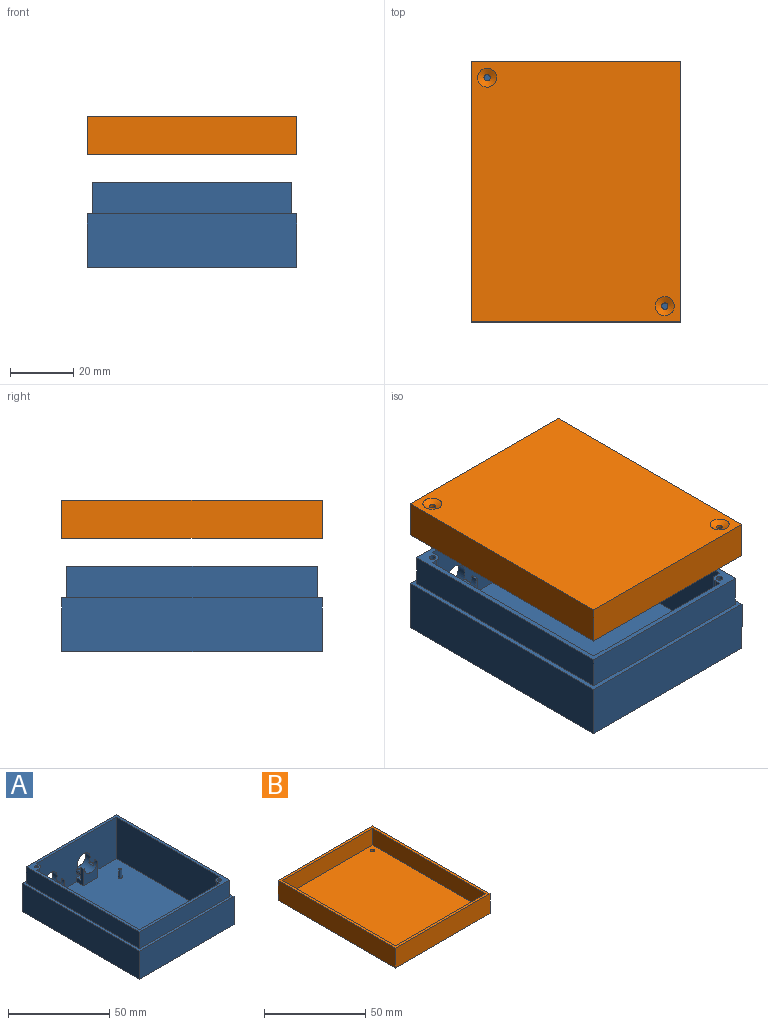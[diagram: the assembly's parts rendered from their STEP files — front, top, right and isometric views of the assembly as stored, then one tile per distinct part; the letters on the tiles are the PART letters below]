
ASSEMBLY  parts=2 mates=1
PART A: 68 faces, bbox 66x82x27 mm
  f0: plane 10x5mm, normal (-1,0,0), area 30.7mm2, adj f6,f7,f10,f11,f40,f46,f47,f49
  f1: plane 10x5mm, normal (1,0,0), area 30.7mm2, adj f6,f10,f11,f37,f39,f46,f47,f57
  f2: plane 10x5mm, normal (-1,0,0), area 30.7mm2, adj f8,f9,f10,f11,f42,f44,f45,f55
  f3: plane 10x5mm, normal (1,0,0), area 30.7mm2, adj f8,f10,f11,f38,f41,f44,f45,f50
  f4: cylinder r=4.5mm len=9mm, axis (0,-1,0), area 137.2mm2, adj f8,f9,f11,f35,f38,f41,f42,f53
  f5: cylinder r=4.5mm len=9mm, axis (0,-1,0), area 137.2mm2, adj f6,f7,f11,f35,f37,f39,f40,f51
  f6: plane 10x10mm, normal (0,-1,0), area 68.2mm2, adj f0,f1,f5,f7,f10,f37
  f7: plane 2x0.5mm, normal (0,0,1), area 1mm2, adj f0,f5,f6,f40
  f8: plane 10x10mm, normal (0,-1,0), area 68.2mm2, adj f2,f3,f4,f9,f10,f38
  f9: plane 2x0.5mm, normal (0,0,1), area 1mm2, adj f2,f4,f8,f42
  f10: plane 76x60mm, normal (0,0,1), area 4417.2mm2, adj f0,f1,f2,f3,f6,f8,f11,f12
  f11: plane 56x25mm, normal (0,-1,0), area 1185.4mm2, adj f0,f1,f2,f3,f4,f5,f10,f20
  f12: cone r=1mm half-angle=3deg, axis (0,0,-1), area 27.3mm2, adj f10,f13
  f13: plane 1.48x1.48mm, normal (0,0,1), area 1.7mm2, adj f12
  f14: cone r=1mm half-angle=3deg, axis (0,0,-1), area 27.3mm2, adj f10,f15
  f15: plane 1.48x1.48mm, normal (0,0,1), area 1.7mm2, adj f14
  f16: cone r=1mm half-angle=3deg, axis (0,0,-1), area 27.3mm2, adj f10,f17
  f17: plane 1.48x1.48mm, normal (0,0,1), area 1.7mm2, adj f16
  f18: cone r=1mm half-angle=3deg, axis (0,0,-1), area 27.3mm2, adj f10,f19
  f19: plane 1.48x1.48mm, normal (0,0,1), area 1.7mm2, adj f18
  f20: plane 25x2mm, normal (1,0,0), area 50mm2, adj f10,f11,f29,f61
  f21: plane 72x25mm, normal (-1,0,0), area 1800mm2, adj f10,f11,f22,f29
  f22: plane 25x2mm, normal (0,1,0), area 50mm2, adj f10,f21,f29,f62
  f23: plane 25x2mm, normal (-1,0,0), area 50mm2, adj f10,f24,f29,f62
  f24: plane 56x25mm, normal (0,1,0), area 1400mm2, adj f10,f23,f25,f29
  f25: plane 72x25mm, normal (1,0,0), area 1800mm2, adj f10,f24,f27,f29
  f26: cylinder r=1mm len=25mm, axis (0,0,-1), area 157.1mm2, adj f29,f31
  f27: plane 25x2mm, normal (0,-1,0), area 50mm2, adj f10,f25,f29,f61
  f28: cylinder r=1mm len=25mm, axis (0,0,-1), area 157.1mm2, adj f29,f30
  f29: plane 79x63mm, normal (0,0,1), area 441mm2, adj f11,f20,f21,f22,f23,f24,f25,f26
  f30: plane 2x2mm, normal (0,0,1), area 3.1mm2, adj f28
  f31: plane 2x2mm, normal (0,0,1), area 3.1mm2, adj f26
  f32: plane 82x66mm, normal (0,0,-1), area 5412mm2, adj f33,f34,f35,f36
  f33: plane 66x17mm, normal (0,-1,0), area 1122mm2, adj f32,f34,f36,f67
  f34: plane 82x17mm, normal (-1,0,0), area 1394mm2, adj f32,f33,f35,f67
  f35: plane 66x17mm, normal (0,1,0), area 994.8mm2, adj f4,f5,f32,f34,f36,f67
  f36: plane 82x17mm, normal (1,0,0), area 1394mm2, adj f32,f33,f35,f67
  f37: plane 2x0.5mm, normal (0,0,1), area 1mm2, adj f1,f5,f6,f39
  f38: plane 2x0.5mm, normal (0,0,1), area 1mm2, adj f3,f4,f8,f41
  f39: plane 3.45x1.5mm, normal (0,1,0), area 2mm2, adj f1,f5,f37,f57,f58
  f40: plane 3.45x1.5mm, normal (0,1,0), area 2mm2, adj f0,f5,f7,f51,f52
  f41: plane 3.45x1.5mm, normal (0,1,0), area 2mm2, adj f3,f4,f38,f53,f54
  f42: plane 3.45x1.5mm, normal (0,1,0), area 2mm2, adj f2,f4,f9,f55,f56
  f43: plane 8x3mm, normal (0,0,-1), area 24mm2, adj f11,f45,f50,f60
  f44: plane 10x3mm, normal (0,0,1), area 30mm2, adj f2,f3,f11,f45
  f45: plane 10x3mm, normal (0,1,0), area 20.4mm2, adj f2,f3,f43,f44,f50,f60
  f46: plane 10x3mm, normal (0,1,0), area 20.4mm2, adj f0,f1,f47,f48,f49,f59
  f47: plane 10x3mm, normal (0,0,1), area 30mm2, adj f0,f1,f11,f46
  f48: plane 8x3mm, normal (0,0,-1), area 24mm2, adj f11,f46,f49,f59
  f49: cylinder r=1mm len=3mm, axis (0,-1,0), area 4.7mm2, adj f0,f11,f46,f48
  f50: cylinder r=1mm len=3mm, axis (0,1,0), area 4.7mm2, adj f3,f11,f43,f45
  f51: cylinder r=1mm len=3mm, axis (0,-1,0), area 2.3mm2, adj f5,f11,f40,f52
  f52: cylinder r=1mm len=3mm, axis (0,1,0), area 4.3mm2, adj f0,f11,f40,f51
  f53: cylinder r=1mm len=3mm, axis (0,-1,0), area 2.3mm2, adj f4,f11,f41,f54
  f54: cylinder r=1mm len=3mm, axis (0,-1,0), area 4.3mm2, adj f3,f11,f41,f53
  f55: cylinder r=1mm len=3mm, axis (0,1,0), area 4.3mm2, adj f2,f11,f42,f56
  f56: cylinder r=1mm len=3mm, axis (0,-1,0), area 2.3mm2, adj f4,f11,f42,f55
  f57: cylinder r=1mm len=3mm, axis (0,-1,0), area 4.3mm2, adj f1,f11,f39,f58
  f58: cylinder r=1mm len=3mm, axis (0,-1,0), area 2.3mm2, adj f5,f11,f39,f57
  f59: cylinder r=1mm len=3mm, axis (0,1,0), area 4.7mm2, adj f1,f11,f46,f48
  f60: cylinder r=1mm len=3mm, axis (0,-1,0), area 4.7mm2, adj f2,f11,f43,f45
  f61: cylinder r=2mm len=25mm, axis (0,0,1), area 78.5mm2, adj f10,f20,f27,f29
  f62: cylinder r=2mm len=25mm, axis (0,0,1), area 78.5mm2, adj f10,f22,f23,f29
  f63: plane 79x10mm, normal (-1,0,0), area 790mm2, adj f29,f64,f66,f67
  f64: plane 63x10mm, normal (0,1,0), area 630mm2, adj f29,f63,f65,f67
  f65: plane 79x10mm, normal (1,0,0), area 790mm2, adj f29,f64,f66,f67
  f66: plane 63x10mm, normal (0,-1,0), area 630mm2, adj f29,f63,f65,f67
  f67: plane 82x66mm, normal (0,0,1), area 435mm2, adj f33,f34,f35,f36,f63,f64,f65,f66
PART B: 15 faces, bbox 66x82x12 mm
  f0: plane 79x10mm, normal (1,0,0), area 790mm2, adj f1,f7,f8,f9
  f1: plane 63x10mm, normal (0,-1,0), area 630mm2, adj f0,f2,f8,f9
  f2: plane 79x10mm, normal (-1,0,0), area 790mm2, adj f1,f7,f8,f9
  f3: plane 82x12mm, normal (-1,0,0), area 984mm2, adj f4,f6,f8,f12
  f4: plane 66x12mm, normal (0,-1,0), area 792mm2, adj f3,f5,f8,f12
  f5: plane 82x12mm, normal (1,0,0), area 984mm2, adj f4,f6,f8,f12
  f6: plane 66x12mm, normal (0,1,0), area 792mm2, adj f3,f5,f8,f12
  f7: plane 63x10mm, normal (0,1,0), area 630mm2, adj f0,f2,f8,f9
  f8: plane 82x66mm, normal (0,0,1), area 435mm2, adj f0,f1,f2,f3,f4,f5,f6,f7
  f9: plane 79x63mm, normal (0,0,1), area 4970.7mm2, adj f0,f1,f2,f7,f10,f11
  f10: cylinder r=1mm len=2mm, axis (0,0,1), area 6.3mm2, adj f9,f13
  f11: cylinder r=1mm len=2mm, axis (0,0,1), area 6.3mm2, adj f9,f14
  f12: plane 82x66mm, normal (0,0,-1), area 5355.5mm2, adj f3,f4,f5,f6,f13,f14
  f13: cone r=3mm half-angle=63.4deg, axis (0,0,-1), area 28.1mm2, adj f10,f12
  f14: cone r=3mm half-angle=63.4deg, axis (0,0,-1), area 28.1mm2, adj f11,f12
PLACE A rot(axis=(0,1,0),0deg) t=(-4.2,83.22,55.1)mm
PLACE B rot(axis=(0,-1,0),180deg) t=(-30.78,96.4,98.86)mm
MATE slider A.f67 <-> B.f8  axis (0,0,1) through (18.05,95.91,70.1)mm
